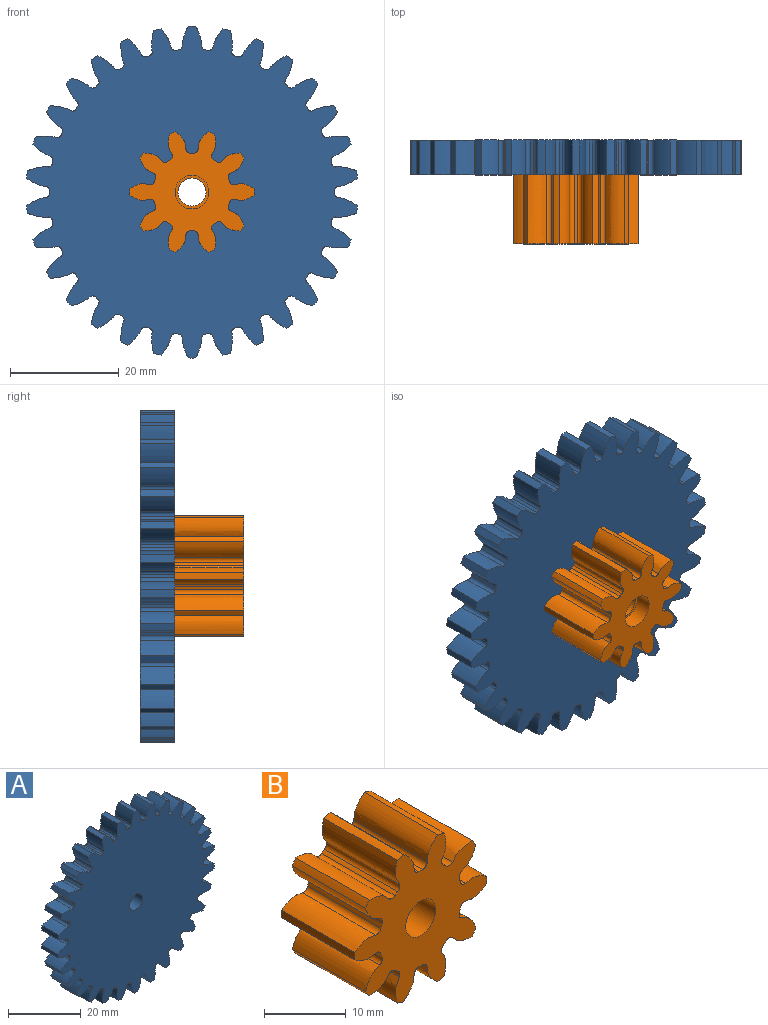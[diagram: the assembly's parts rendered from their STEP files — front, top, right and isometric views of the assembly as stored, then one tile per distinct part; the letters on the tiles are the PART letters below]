
ASSEMBLY  parts=2 mates=1
PART A: 185 faces, bbox 60.8x6.4x61 mm
  f0: cylinder r=2.59mm len=5.18mm, axis (0,-1,0), area 54.5mm2, adj f30,f183
  f1: cylinder r=30.48mm len=6.35mm, axis (0,1,0), area 8.9mm2, adj f30,f32,f173,f180
  f2: cylinder r=30.48mm len=6.35mm, axis (0,1,0), area 8.9mm2, adj f30,f32,f168,f175
  f3: cylinder r=30.48mm len=6.35mm, axis (0,1,0), area 8.9mm2, adj f30,f32,f163,f170
  f4: cylinder r=30.48mm len=6.35mm, axis (0,1,0), area 8.9mm2, adj f30,f32,f153,f165
  f5: cylinder r=30.48mm len=6.35mm, axis (0,1,0), area 8.9mm2, adj f30,f32,f148,f160
  f6: cylinder r=30.48mm len=6.35mm, axis (0,1,0), area 8.9mm2, adj f30,f32,f155,f158
  f7: cylinder r=30.48mm len=6.35mm, axis (0,1,0), area 8.9mm2, adj f30,f32,f143,f150
  f8: cylinder r=30.48mm len=6.35mm, axis (0,1,0), area 8.9mm2, adj f30,f32,f33,f145
  f9: cylinder r=30.48mm len=6.35mm, axis (0,1,0), area 8.9mm2, adj f30,f32,f128,f140
  f10: cylinder r=30.48mm len=6.35mm, axis (0,1,0), area 8.9mm2, adj f30,f32,f135,f138
  f11: cylinder r=30.48mm len=6.35mm, axis (0,1,0), area 8.9mm2, adj f30,f32,f123,f130
  f12: cylinder r=30.48mm len=6.35mm, axis (0,1,0), area 8.9mm2, adj f30,f32,f125,f178
  f13: cylinder r=30.48mm len=6.35mm, axis (0,1,0), area 8.9mm2, adj f30,f32,f120,f133
  f14: cylinder r=30.48mm len=6.35mm, axis (0,1,0), area 8.9mm2, adj f30,f32,f115,f118
  f15: cylinder r=30.48mm len=6.35mm, axis (0,1,0), area 8.9mm2, adj f30,f32,f110,f113
  f16: cylinder r=30.48mm len=6.35mm, axis (0,1,0), area 8.9mm2, adj f30,f32,f105,f108
  f17: cylinder r=30.48mm len=6.35mm, axis (0,1,0), area 8.9mm2, adj f30,f32,f88,f100
  f18: cylinder r=30.48mm len=6.35mm, axis (0,1,0), area 8.9mm2, adj f30,f32,f95,f98
  f19: cylinder r=30.48mm len=6.35mm, axis (0,1,0), area 8.9mm2, adj f30,f32,f83,f90
  f20: cylinder r=30.48mm len=6.35mm, axis (0,1,0), area 8.9mm2, adj f30,f32,f85,f103
  f21: cylinder r=30.48mm len=6.35mm, axis (0,1,0), area 8.9mm2, adj f30,f32,f80,f93
  f22: cylinder r=30.48mm len=6.35mm, axis (0,1,0), area 8.9mm2, adj f30,f32,f75,f78
  f23: cylinder r=30.48mm len=6.35mm, axis (0,1,0), area 8.9mm2, adj f30,f32,f70,f73
  f24: cylinder r=30.48mm len=6.35mm, axis (0,1,0), area 8.9mm2, adj f30,f32,f65,f68
  f25: cylinder r=30.48mm len=6.35mm, axis (0,1,0), area 8.9mm2, adj f30,f32,f53,f60
  f26: cylinder r=30.48mm len=6.35mm, axis (0,1,0), area 8.9mm2, adj f30,f32,f43,f55
  f27: cylinder r=30.48mm len=6.35mm, axis (0,1,0), area 8.9mm2, adj f30,f32,f50,f63
  f28: cylinder r=30.48mm len=6.35mm, axis (0,1,0), area 8.9mm2, adj f30,f32,f45,f48
  f29: cylinder r=30.48mm len=6.35mm, axis (0,1,0), area 8.9mm2, adj f30,f32,f40,f58
  f30: plane 60.96x60.76mm, normal (0,-1,0), area 2515.4mm2, adj f0,f1,f2,f3,f4,f5,f6,f7
  f31: cylinder r=30.48mm len=6.35mm, axis (0,1,0), area 8.9mm2, adj f30,f32,f35,f38
  f32: plane 60.96x60.76mm, normal (0,1,0), area 2506.3mm2, adj f1,f2,f3,f4,f5,f6,f7,f8
  f33: extruded ~6.35x3.53mm, area 24.5mm2, adj f8,f30,f32,f36
  f34: cylinder r=26.19mm len=6.35mm, axis (0,1,0), area 3.8mm2, adj f30,f32,f36,f37
  f35: extruded ~6.35x3.53mm, area 24.5mm2, adj f30,f31,f32,f37
  f36: cylinder r=0.7mm len=6.35mm, axis (0,1,0), area 6.8mm2, adj f30,f32,f33,f34
  f37: cylinder r=0.7mm len=6.35mm, axis (0,1,0), area 6.8mm2, adj f30,f32,f34,f35
  f38: extruded ~6.35x3.76mm, area 24.5mm2, adj f30,f31,f32,f41
  f39: cylinder r=26.19mm len=6.35mm, axis (0,1,0), area 3.8mm2, adj f30,f32,f41,f42
  f40: extruded ~6.35x3.15mm, area 24.5mm2, adj f29,f30,f32,f42
  f41: cylinder r=0.7mm len=6.35mm, axis (0,1,0), area 6.8mm2, adj f30,f32,f38,f39
  f42: cylinder r=0.7mm len=6.35mm, axis (0,1,0), area 6.8mm2, adj f30,f32,f39,f40
  f43: extruded ~6.35x3.46mm, area 24.5mm2, adj f26,f30,f32,f46
  f44: cylinder r=26.19mm len=6.35mm, axis (0,1,0), area 3.8mm2, adj f30,f32,f46,f47
  f45: extruded ~6.35x3.62mm, area 24.5mm2, adj f28,f30,f32,f47
  f46: cylinder r=0.7mm len=6.35mm, axis (0,1,0), area 6.8mm2, adj f30,f32,f43,f44
  f47: cylinder r=0.7mm len=6.35mm, axis (0,1,0), area 6.8mm2, adj f30,f32,f44,f45
  f48: extruded ~6.35x3.05mm, area 24.5mm2, adj f28,f30,f32,f51
  f49: cylinder r=26.19mm len=6.35mm, axis (0,1,0), area 3.8mm2, adj f30,f32,f51,f52
  f50: extruded ~6.35x3.8mm, area 24.5mm2, adj f27,f30,f32,f52
  f51: cylinder r=0.7mm len=6.35mm, axis (0,1,0), area 6.8mm2, adj f30,f32,f48,f49
  f52: cylinder r=0.7mm len=6.35mm, axis (0,1,0), area 6.8mm2, adj f30,f32,f49,f50
  f53: extruded ~6.35x3.73mm, area 24.5mm2, adj f25,f30,f32,f56
  f54: cylinder r=26.19mm len=6.35mm, axis (0,1,0), area 3.8mm2, adj f30,f32,f56,f57
  f55: extruded ~6.35x3.27mm, area 24.5mm2, adj f26,f30,f32,f57
  f56: cylinder r=0.7mm len=6.35mm, axis (0,1,0), area 6.8mm2, adj f30,f32,f53,f54
  f57: cylinder r=0.7mm len=6.35mm, axis (0,1,0), area 6.8mm2, adj f30,f32,f54,f55
  f58: extruded ~6.35x3.83mm, area 24.5mm2, adj f29,f30,f32,f61
  f59: cylinder r=26.19mm len=6.35mm, axis (0,1,0), area 3.8mm2, adj f30,f32,f61,f62
  f60: extruded ~6.35x2.79mm, area 24.5mm2, adj f25,f30,f32,f62
  f61: cylinder r=0.7mm len=6.35mm, axis (0,1,0), area 6.8mm2, adj f30,f32,f58,f59
  f62: cylinder r=0.7mm len=6.35mm, axis (0,1,0), area 6.8mm2, adj f30,f32,f59,f60
  f63: extruded ~6.35x2.9mm, area 24.5mm2, adj f27,f30,f32,f66
  f64: cylinder r=26.19mm len=6.35mm, axis (0,1,0), area 3.8mm2, adj f30,f32,f66,f67
  f65: extruded ~6.35x3.82mm, area 24.5mm2, adj f24,f30,f32,f67
  f66: cylinder r=0.7mm len=6.35mm, axis (0,1,0), area 6.8mm2, adj f30,f32,f63,f64
  f67: cylinder r=0.7mm len=6.35mm, axis (0,1,0), area 6.8mm2, adj f30,f32,f64,f65
  f68: extruded ~6.35x3.36mm, area 24.5mm2, adj f24,f30,f32,f71
  f69: cylinder r=26.19mm len=6.35mm, axis (0,1,0), area 3.8mm2, adj f30,f32,f71,f72
  f70: extruded ~6.35x3.67mm, area 24.5mm2, adj f23,f30,f32,f72
  f71: cylinder r=0.7mm len=6.35mm, axis (0,1,0), area 6.8mm2, adj f30,f32,f68,f69
  f72: cylinder r=0.7mm len=6.35mm, axis (0,1,0), area 6.8mm2, adj f30,f32,f69,f70
  f73: extruded ~6.35x3.67mm, area 24.5mm2, adj f23,f30,f32,f76
  f74: cylinder r=26.19mm len=6.35mm, axis (0,1,0), area 3.8mm2, adj f30,f32,f76,f77
  f75: extruded ~6.35x3.36mm, area 24.5mm2, adj f22,f30,f32,f77
  f76: cylinder r=0.7mm len=6.35mm, axis (0,1,0), area 6.8mm2, adj f30,f32,f73,f74
  f77: cylinder r=0.7mm len=6.35mm, axis (0,1,0), area 6.8mm2, adj f30,f32,f74,f75
  f78: extruded ~6.35x3.82mm, area 24.5mm2, adj f22,f30,f32,f81
  f79: cylinder r=26.19mm len=6.35mm, axis (0,1,0), area 3.8mm2, adj f30,f32,f81,f82
  f80: extruded ~6.35x2.9mm, area 24.5mm2, adj f21,f30,f32,f82
  f81: cylinder r=0.7mm len=6.35mm, axis (0,1,0), area 6.8mm2, adj f30,f32,f78,f79
  f82: cylinder r=0.7mm len=6.35mm, axis (0,1,0), area 6.8mm2, adj f30,f32,f79,f80
  f83: extruded ~6.35x2.79mm, area 24.5mm2, adj f19,f30,f32,f86
  f84: cylinder r=26.19mm len=6.35mm, axis (0,1,0), area 3.8mm2, adj f30,f32,f86,f87
  f85: extruded ~6.35x3.83mm, area 24.5mm2, adj f20,f30,f32,f87
  f86: cylinder r=0.7mm len=6.35mm, axis (0,1,0), area 6.8mm2, adj f30,f32,f83,f84
  f87: cylinder r=0.7mm len=6.35mm, axis (0,1,0), area 6.8mm2, adj f30,f32,f84,f85
  f88: extruded ~6.35x3.27mm, area 24.5mm2, adj f17,f30,f32,f91
  f89: cylinder r=26.19mm len=6.35mm, axis (0,1,0), area 3.8mm2, adj f30,f32,f91,f92
  f90: extruded ~6.35x3.73mm, area 24.5mm2, adj f19,f30,f32,f92
  f91: cylinder r=0.7mm len=6.35mm, axis (0,1,0), area 6.8mm2, adj f30,f32,f88,f89
  f92: cylinder r=0.7mm len=6.35mm, axis (0,1,0), area 6.8mm2, adj f30,f32,f89,f90
  f93: extruded ~6.35x3.8mm, area 24.5mm2, adj f21,f30,f32,f96
  f94: cylinder r=26.19mm len=6.35mm, axis (0,1,0), area 3.8mm2, adj f30,f32,f96,f97
  f95: extruded ~6.35x3.05mm, area 24.5mm2, adj f18,f30,f32,f97
  f96: cylinder r=0.7mm len=6.35mm, axis (0,1,0), area 6.8mm2, adj f30,f32,f93,f94
  f97: cylinder r=0.7mm len=6.35mm, axis (0,1,0), area 6.8mm2, adj f30,f32,f94,f95
  f98: extruded ~6.35x3.62mm, area 24.5mm2, adj f18,f30,f32,f101
  f99: cylinder r=26.19mm len=6.35mm, axis (0,1,0), area 3.8mm2, adj f30,f32,f101,f102
  f100: extruded ~6.35x3.46mm, area 24.5mm2, adj f17,f30,f32,f102
  f101: cylinder r=0.7mm len=6.35mm, axis (0,1,0), area 6.8mm2, adj f30,f32,f98,f99
  f102: cylinder r=0.7mm len=6.35mm, axis (0,1,0), area 6.8mm2, adj f30,f32,f99,f100
  f103: extruded ~6.35x3.15mm, area 24.5mm2, adj f20,f30,f32,f106
  f104: cylinder r=26.19mm len=6.35mm, axis (0,1,0), area 3.8mm2, adj f30,f32,f106,f107
  f105: extruded ~6.35x3.76mm, area 24.5mm2, adj f16,f30,f32,f107
  f106: cylinder r=0.7mm len=6.35mm, axis (0,1,0), area 6.8mm2, adj f30,f32,f103,f104
  f107: cylinder r=0.7mm len=6.35mm, axis (0,1,0), area 6.8mm2, adj f30,f32,f104,f105
  f108: extruded ~6.35x3.53mm, area 24.5mm2, adj f16,f30,f32,f111
  f109: cylinder r=26.19mm len=6.35mm, axis (0,1,0), area 3.8mm2, adj f30,f32,f111,f112
  f110: extruded ~6.35x3.53mm, area 24.5mm2, adj f15,f30,f32,f112
  f111: cylinder r=0.7mm len=6.35mm, axis (0,1,0), area 6.8mm2, adj f30,f32,f108,f109
  f112: cylinder r=0.7mm len=6.35mm, axis (0,1,0), area 6.8mm2, adj f30,f32,f109,f110
  f113: extruded ~6.35x3.76mm, area 24.5mm2, adj f15,f30,f32,f116
  f114: cylinder r=26.19mm len=6.35mm, axis (0,1,0), area 3.8mm2, adj f30,f32,f116,f117
  f115: extruded ~6.35x3.15mm, area 24.5mm2, adj f14,f30,f32,f117
  f116: cylinder r=0.7mm len=6.35mm, axis (0,1,0), area 6.8mm2, adj f30,f32,f113,f114
  f117: cylinder r=0.7mm len=6.35mm, axis (0,1,0), area 6.8mm2, adj f30,f32,f114,f115
  f118: extruded ~6.35x3.83mm, area 24.5mm2, adj f14,f30,f32,f121
  f119: cylinder r=26.19mm len=6.35mm, axis (0,1,0), area 3.8mm2, adj f30,f32,f121,f122
  f120: extruded ~6.35x2.79mm, area 24.5mm2, adj f13,f30,f32,f122
  f121: cylinder r=0.7mm len=6.35mm, axis (0,1,0), area 6.8mm2, adj f30,f32,f118,f119
  f122: cylinder r=0.7mm len=6.35mm, axis (0,1,0), area 6.8mm2, adj f30,f32,f119,f120
  f123: extruded ~6.35x2.9mm, area 24.5mm2, adj f11,f30,f32,f126
  f124: cylinder r=26.19mm len=6.35mm, axis (0,1,0), area 3.8mm2, adj f30,f32,f126,f127
  f125: extruded ~6.35x3.82mm, area 24.5mm2, adj f12,f30,f32,f127
  f126: cylinder r=0.7mm len=6.35mm, axis (0,1,0), area 6.8mm2, adj f30,f32,f123,f124
  f127: cylinder r=0.7mm len=6.35mm, axis (0,1,0), area 6.8mm2, adj f30,f32,f124,f125
  f128: extruded ~6.35x3.05mm, area 24.5mm2, adj f9,f30,f32,f131
  f129: cylinder r=26.19mm len=6.35mm, axis (0,1,0), area 3.8mm2, adj f30,f32,f131,f132
  f130: extruded ~6.35x3.8mm, area 24.5mm2, adj f11,f30,f32,f132
  f131: cylinder r=0.7mm len=6.35mm, axis (0,1,0), area 6.8mm2, adj f30,f32,f128,f129
  f132: cylinder r=0.7mm len=6.35mm, axis (0,1,0), area 6.8mm2, adj f30,f32,f129,f130
  f133: extruded ~6.35x3.73mm, area 24.5mm2, adj f13,f30,f32,f136
  f134: cylinder r=26.19mm len=6.35mm, axis (0,1,0), area 3.8mm2, adj f30,f32,f136,f137
  f135: extruded ~6.35x3.27mm, area 24.5mm2, adj f10,f30,f32,f137
  f136: cylinder r=0.7mm len=6.35mm, axis (0,1,0), area 6.8mm2, adj f30,f32,f133,f134
  f137: cylinder r=0.7mm len=6.35mm, axis (0,1,0), area 6.8mm2, adj f30,f32,f134,f135
  f138: extruded ~6.35x3.46mm, area 24.5mm2, adj f10,f30,f32,f141
  f139: cylinder r=26.19mm len=6.35mm, axis (0,1,0), area 3.8mm2, adj f30,f32,f141,f142
  f140: extruded ~6.35x3.62mm, area 24.5mm2, adj f9,f30,f32,f142
  f141: cylinder r=0.7mm len=6.35mm, axis (0,1,0), area 6.8mm2, adj f30,f32,f138,f139
  f142: cylinder r=0.7mm len=6.35mm, axis (0,1,0), area 6.8mm2, adj f30,f32,f139,f140
  f143: extruded ~6.35x3.15mm, area 24.5mm2, adj f7,f30,f32,f146
  f144: cylinder r=26.19mm len=6.35mm, axis (0,1,0), area 3.8mm2, adj f30,f32,f146,f147
  f145: extruded ~6.35x3.76mm, area 24.5mm2, adj f8,f30,f32,f147
  f146: cylinder r=0.7mm len=6.35mm, axis (0,1,0), area 6.8mm2, adj f30,f32,f143,f144
  f147: cylinder r=0.7mm len=6.35mm, axis (0,1,0), area 6.8mm2, adj f30,f32,f144,f145
  f148: extruded ~6.35x2.79mm, area 24.5mm2, adj f5,f30,f32,f151
  f149: cylinder r=26.19mm len=6.35mm, axis (0,1,0), area 3.8mm2, adj f30,f32,f151,f152
  f150: extruded ~6.35x3.83mm, area 24.5mm2, adj f7,f30,f32,f152
  f151: cylinder r=0.7mm len=6.35mm, axis (0,1,0), area 6.8mm2, adj f30,f32,f148,f149
  f152: cylinder r=0.7mm len=6.35mm, axis (0,1,0), area 6.8mm2, adj f30,f32,f149,f150
  f153: extruded ~6.35x3.62mm, area 24.5mm2, adj f4,f30,f32,f156
  f154: cylinder r=26.19mm len=6.35mm, axis (0,1,0), area 3.8mm2, adj f30,f32,f156,f157
  f155: extruded ~6.35x3.46mm, area 24.5mm2, adj f6,f30,f32,f157
  f156: cylinder r=0.7mm len=6.35mm, axis (0,1,0), area 6.8mm2, adj f30,f32,f153,f154
  f157: cylinder r=0.7mm len=6.35mm, axis (0,1,0), area 6.8mm2, adj f30,f32,f154,f155
  f158: extruded ~6.35x3.27mm, area 24.5mm2, adj f6,f30,f32,f161
  f159: cylinder r=26.19mm len=6.35mm, axis (0,1,0), area 3.8mm2, adj f30,f32,f161,f162
  f160: extruded ~6.35x3.73mm, area 24.5mm2, adj f5,f30,f32,f162
  f161: cylinder r=0.7mm len=6.35mm, axis (0,1,0), area 6.8mm2, adj f30,f32,f158,f159
  f162: cylinder r=0.7mm len=6.35mm, axis (0,1,0), area 6.8mm2, adj f30,f32,f159,f160
  f163: extruded ~6.35x3.8mm, area 24.5mm2, adj f3,f30,f32,f166
  f164: cylinder r=26.19mm len=6.35mm, axis (0,1,0), area 3.8mm2, adj f30,f32,f166,f167
  f165: extruded ~6.35x3.05mm, area 24.5mm2, adj f4,f30,f32,f167
  f166: cylinder r=0.7mm len=6.35mm, axis (0,1,0), area 6.8mm2, adj f30,f32,f163,f164
  f167: cylinder r=0.7mm len=6.35mm, axis (0,1,0), area 6.8mm2, adj f30,f32,f164,f165
  f168: extruded ~6.35x3.82mm, area 24.5mm2, adj f2,f30,f32,f171
  f169: cylinder r=26.19mm len=6.35mm, axis (0,1,0), area 3.8mm2, adj f30,f32,f171,f172
  f170: extruded ~6.35x2.9mm, area 24.5mm2, adj f3,f30,f32,f172
  f171: cylinder r=0.7mm len=6.35mm, axis (0,1,0), area 6.8mm2, adj f30,f32,f168,f169
  f172: cylinder r=0.7mm len=6.35mm, axis (0,1,0), area 6.8mm2, adj f30,f32,f169,f170
  f173: extruded ~6.35x3.67mm, area 24.5mm2, adj f1,f30,f32,f176
  f174: cylinder r=26.19mm len=6.35mm, axis (0,1,0), area 3.8mm2, adj f30,f32,f176,f177
  f175: extruded ~6.35x3.36mm, area 24.5mm2, adj f2,f30,f32,f177
  f176: cylinder r=0.7mm len=6.35mm, axis (0,1,0), area 6.8mm2, adj f30,f32,f173,f174
  f177: cylinder r=0.7mm len=6.35mm, axis (0,1,0), area 6.8mm2, adj f30,f32,f174,f175
  f178: extruded ~6.35x3.36mm, area 24.5mm2, adj f12,f30,f32,f181
  f179: cylinder r=26.19mm len=6.35mm, axis (0,1,0), area 3.8mm2, adj f30,f32,f181,f182
  f180: extruded ~6.35x3.67mm, area 24.5mm2, adj f1,f30,f32,f182
  f181: cylinder r=0.7mm len=6.35mm, axis (0,1,0), area 6.8mm2, adj f30,f32,f178,f179
  f182: cylinder r=0.7mm len=6.35mm, axis (0,1,0), area 6.8mm2, adj f30,f32,f179,f180
  f183: plane 6.2x6.2mm, normal (0,1,0), area 9.1mm2, adj f0,f184
  f184: cylinder r=3.1mm len=6.2mm, axis (0,1,0), area 58.4mm2, adj f32,f183
PART B: 65 faces, bbox 22.9x12.7x22.1 mm
  f0: cylinder r=2.58mm len=9.7mm, axis (0,-1,0), area 157.5mm2, adj f10,f63
  f1: cylinder r=11.43mm len=12.7mm, axis (0,1,0), area 14.2mm2, adj f10,f12,f15,f59
  f2: cylinder r=11.43mm len=12.7mm, axis (0,1,0), area 14.2mm2, adj f10,f12,f54,f60
  f3: cylinder r=11.43mm len=12.7mm, axis (0,1,0), area 14.2mm2, adj f10,f12,f45,f49
  f4: cylinder r=11.43mm len=12.7mm, axis (0,1,0), area 14.2mm2, adj f10,f12,f44,f55
  f5: cylinder r=11.43mm len=12.7mm, axis (0,1,0), area 14.2mm2, adj f10,f12,f35,f39
  f6: cylinder r=11.43mm len=12.7mm, axis (0,1,0), area 14.2mm2, adj f10,f12,f34,f50
  f7: cylinder r=11.43mm len=12.7mm, axis (0,1,0), area 14.2mm2, adj f10,f12,f29,f40
  f8: cylinder r=11.43mm len=12.7mm, axis (0,1,0), area 14.2mm2, adj f10,f12,f24,f30
  f9: cylinder r=11.43mm len=12.7mm, axis (0,1,0), area 14.2mm2, adj f10,f12,f19,f25
  f10: plane 22.9x22.11mm, normal (0,-1,0), area 251.7mm2, adj f0,f1,f2,f3,f4,f5,f6,f7
  f11: cylinder r=11.43mm len=12.7mm, axis (0,1,0), area 14.2mm2, adj f10,f12,f14,f20
  f12: plane 22.9x22.11mm, normal (0,1,0), area 242.4mm2, adj f1,f2,f3,f4,f5,f6,f7,f8
  f13: cylinder r=7.14mm len=12.7mm, axis (0,1,0), area 7.8mm2, adj f10,f12,f16,f17
  f14: extruded ~12.7x3.64mm, area 49.1mm2, adj f10,f11,f12,f16
  f15: extruded ~12.7x2.78mm, area 49.1mm2, adj f1,f10,f12,f17
  f16: cylinder r=0.78mm len=12.7mm, axis (0,1,0), area 14.7mm2, adj f10,f12,f13,f14
  f17: cylinder r=0.78mm len=12.7mm, axis (0,1,0), area 14.7mm2, adj f10,f12,f13,f15
  f18: cylinder r=7.14mm len=12.7mm, axis (0,1,0), area 7.8mm2, adj f10,f12,f21,f22
  f19: extruded ~12.7x2.78mm, area 49.1mm2, adj f9,f10,f12,f21
  f20: extruded ~12.7x3.64mm, area 49.1mm2, adj f10,f11,f12,f22
  f21: cylinder r=0.78mm len=12.7mm, axis (0,1,0), area 14.7mm2, adj f10,f12,f18,f19
  f22: cylinder r=0.78mm len=12.7mm, axis (0,1,0), area 14.7mm2, adj f10,f12,f18,f20
  f23: cylinder r=7.14mm len=12.7mm, axis (0,1,0), area 7.8mm2, adj f10,f12,f26,f27
  f24: extruded ~12.7x3.71mm, area 49.1mm2, adj f8,f10,f12,f26
  f25: extruded ~12.7x3.41mm, area 49.1mm2, adj f9,f10,f12,f27
  f26: cylinder r=0.78mm len=12.7mm, axis (0,1,0), area 14.7mm2, adj f10,f12,f23,f24
  f27: cylinder r=0.78mm len=12.7mm, axis (0,1,0), area 14.7mm2, adj f10,f12,f23,f25
  f28: cylinder r=7.14mm len=12.7mm, axis (0,1,0), area 7.8mm2, adj f10,f12,f31,f32
  f29: extruded ~12.7x3.22mm, area 49.1mm2, adj f7,f10,f12,f31
  f30: extruded ~12.7x3.22mm, area 49.1mm2, adj f8,f10,f12,f32
  f31: cylinder r=0.78mm len=12.7mm, axis (0,1,0), area 14.7mm2, adj f10,f12,f28,f29
  f32: cylinder r=0.78mm len=12.7mm, axis (0,1,0), area 14.7mm2, adj f10,f12,f28,f30
  f33: cylinder r=7.14mm len=12.7mm, axis (0,1,0), area 7.8mm2, adj f10,f12,f36,f37
  f34: extruded ~12.7x3.64mm, area 49.1mm2, adj f6,f10,f12,f36
  f35: extruded ~12.7x2.78mm, area 49.1mm2, adj f5,f10,f12,f37
  f36: cylinder r=0.78mm len=12.7mm, axis (0,1,0), area 14.7mm2, adj f10,f12,f33,f34
  f37: cylinder r=0.78mm len=12.7mm, axis (0,1,0), area 14.7mm2, adj f10,f12,f33,f35
  f38: cylinder r=7.14mm len=12.7mm, axis (0,1,0), area 7.8mm2, adj f10,f12,f41,f42
  f39: extruded ~12.7x3.41mm, area 49.1mm2, adj f5,f10,f12,f41
  f40: extruded ~12.7x3.71mm, area 49.1mm2, adj f7,f10,f12,f42
  f41: cylinder r=0.78mm len=12.7mm, axis (0,1,0), area 14.7mm2, adj f10,f12,f38,f39
  f42: cylinder r=0.78mm len=12.7mm, axis (0,1,0), area 14.7mm2, adj f10,f12,f38,f40
  f43: cylinder r=7.14mm len=12.7mm, axis (0,1,0), area 7.8mm2, adj f10,f12,f46,f47
  f44: extruded ~12.7x3.71mm, area 49.1mm2, adj f4,f10,f12,f46
  f45: extruded ~12.7x3.41mm, area 49.1mm2, adj f3,f10,f12,f47
  f46: cylinder r=0.78mm len=12.7mm, axis (0,1,0), area 14.7mm2, adj f10,f12,f43,f44
  f47: cylinder r=0.78mm len=12.7mm, axis (0,1,0), area 14.7mm2, adj f10,f12,f43,f45
  f48: cylinder r=7.14mm len=12.7mm, axis (0,1,0), area 7.8mm2, adj f10,f12,f51,f52
  f49: extruded ~12.7x2.78mm, area 49.1mm2, adj f3,f10,f12,f51
  f50: extruded ~12.7x3.64mm, area 49.1mm2, adj f6,f10,f12,f52
  f51: cylinder r=0.78mm len=12.7mm, axis (0,1,0), area 14.7mm2, adj f10,f12,f48,f49
  f52: cylinder r=0.78mm len=12.7mm, axis (0,1,0), area 14.7mm2, adj f10,f12,f48,f50
  f53: cylinder r=7.14mm len=12.7mm, axis (0,1,0), area 7.8mm2, adj f10,f12,f56,f57
  f54: extruded ~12.7x3.22mm, area 49.1mm2, adj f2,f10,f12,f56
  f55: extruded ~12.7x3.22mm, area 49.1mm2, adj f4,f10,f12,f57
  f56: cylinder r=0.78mm len=12.7mm, axis (0,1,0), area 14.7mm2, adj f10,f12,f53,f54
  f57: cylinder r=0.78mm len=12.7mm, axis (0,1,0), area 14.7mm2, adj f10,f12,f53,f55
  f58: cylinder r=7.14mm len=12.7mm, axis (0,1,0), area 7.8mm2, adj f10,f12,f61,f62
  f59: extruded ~12.7x3.41mm, area 49.1mm2, adj f1,f10,f12,f61
  f60: extruded ~12.7x3.71mm, area 49.1mm2, adj f2,f10,f12,f62
  f61: cylinder r=0.78mm len=12.7mm, axis (0,1,0), area 14.7mm2, adj f10,f12,f58,f59
  f62: cylinder r=0.78mm len=12.7mm, axis (0,1,0), area 14.7mm2, adj f10,f12,f58,f60
  f63: plane 6.2x6.2mm, normal (0,1,0), area 9.2mm2, adj f0,f64
  f64: cylinder r=3.1mm len=6.2mm, axis (0,1,0), area 58.4mm2, adj f12,f63
PLACE A at identity fixed
PLACE B rot(axis=(0,0,1),180deg) t=(0,-19.05,0)mm
MATE fastened A.f1 <-> B.f0  axis (0,-1,0) through (0,-6.35,0)mm
